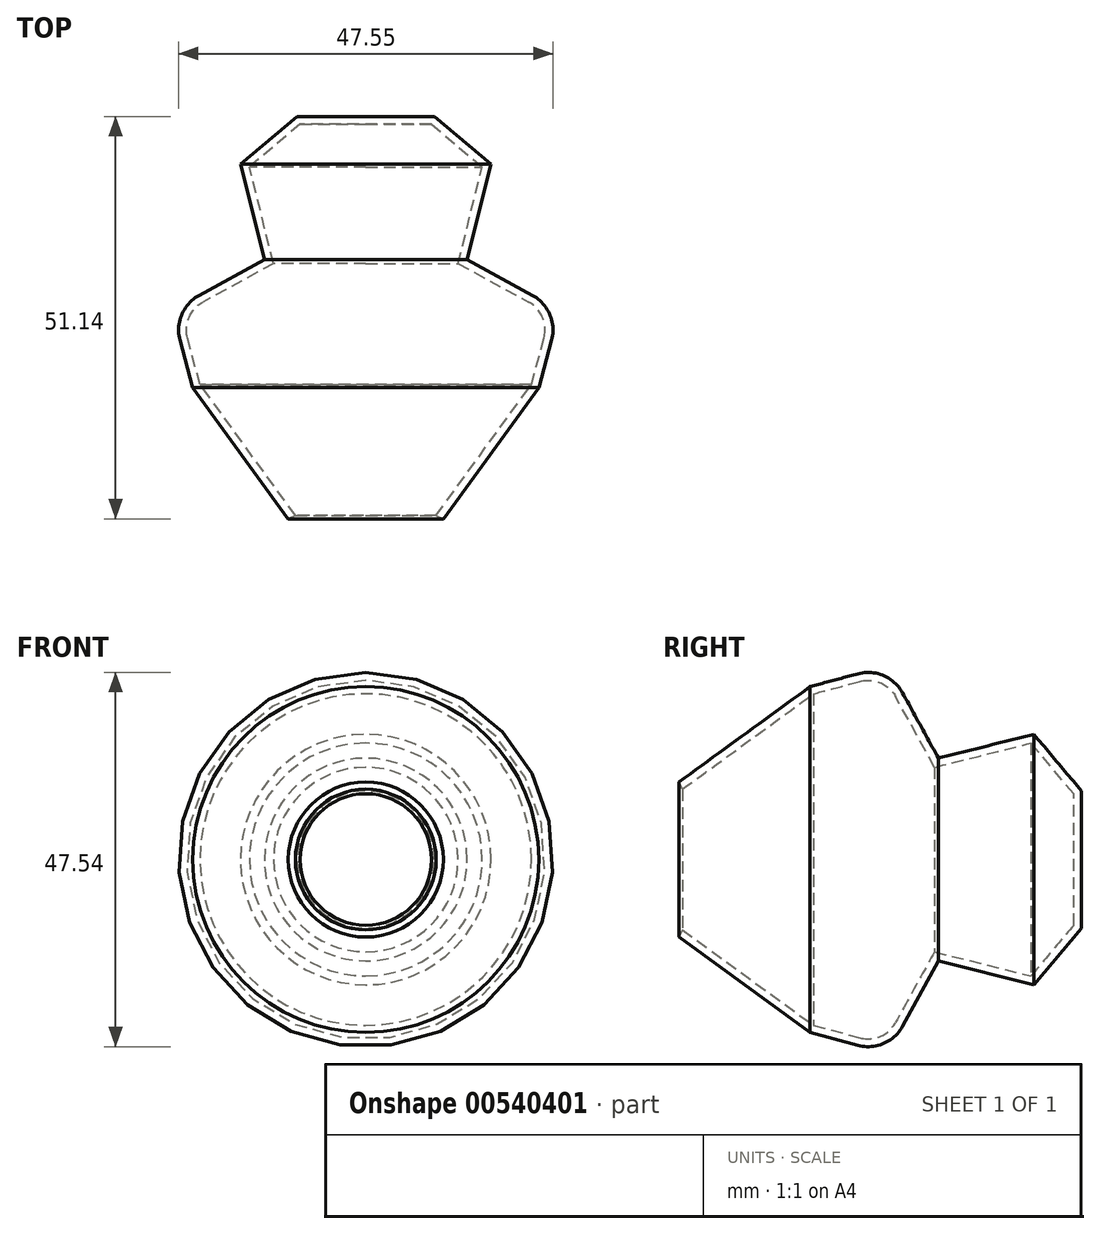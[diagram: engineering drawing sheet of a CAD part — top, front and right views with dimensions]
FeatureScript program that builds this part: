
annotation { "Feature Type Name" : "Feature", "Feature Type Description" : "" }
export const myFeature = defineFeature(function(context is Context, id is Id, definition is map)
    precondition{}
    {
        {
            var Q0;
            Q0=qCreatedBy(makeId("Top.planeOp"),FACE);
            var sketch = newSketch(context, id + "F0", { "sketchPlane" : qUnion([Q0])});
            skLineSegment(sketch, "E0", {"start": v(-38.26, 46.22) * mm, "end": v(-45.46, 40.16) * mm});
            skLineSegment(sketch, "E1", {"start": v(-45.46, 40.16) * mm, "end": v(-42.43, 28.03) * mm});
            skLineSegment(sketch, "E2", {"start": v(-42.43, 28.03) * mm, "end": v(-50.73, 23.48) * mm});
            skLineSegment(sketch, "E3", {"start": v(-53.15, 17.8) * mm, "end": v(-51.52, 11.74) * mm});
            skPoint(sketch, "E4.visualSharp", {"position": v(-54.17, 21.6) * mm});
            skArc(sketch, "E4.filletArc", {"start": v(-50.73, 23.48) * mm, "mid": v(-52.92, 21.06) * mm, "end": v(-53.15, 17.8) * mm});
            skLineSegment(sketch, "E5", {"start": v(-51.52, 11.74) * mm, "end": v(-39.4, -4.92) * mm});
            skLineSegment(sketch, "E6", {"start": v(-38.26, 46.22) * mm, "end": v(-29.55, 46.22) * mm});
            skLineSegment(sketch, "E7", {"start": v(-29.55, 46.22) * mm, "end": v(-29.55, 0) * mm});
            skLineSegment(sketch, "E8", {"start": v(-29.55, 0) * mm, "end": v(-39.4, -4.92) * mm});
            skSolve(sketch);
        }
        {
            var Q0;
            Q0=makeQuery(id+"F0.imprint","IMPRINT",FACE,{"disambiguationData":[TD([[makeQuery(id+"F0.imprint","IMPRINT",EDGE,{"derivedFrom":sQuery(id+"F0.wireOp",EDGE,"E0")}),1.0]])]});
            var Q1;
            Q1=sQuery(id+"F0.wireOp",EDGE,"E7");
            revolve(context, id + "F1", {"entities" : qUnion([Q0]), "axis" : qUnion([Q1]), "revolveType" : RevolveType.FULL});
        }
        {
            var Q0;
            Q0=makeQuery(id+"F1.opRevolve","SWEPT_FACE",FACE,{"disambiguationData":[OSD([sQuery(id+"F0.wireOp",EDGE,"E8")])]});
            shell(context, id + "F2", {"entities" : qUnion([Q0]), "thickness" : 1 * mm});
        }
    });
